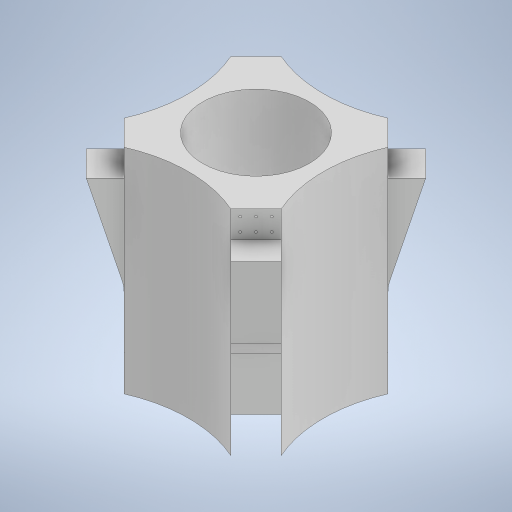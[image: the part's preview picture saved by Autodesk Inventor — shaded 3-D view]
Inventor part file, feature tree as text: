
AUTODESK INVENTOR PART (.ipt)
format: ipt  version: 2023 (Build 270158000, 158)  size: 485,376 bytes
history: native  units: in
note: dims shown in document units (in); Inventor stores cm internally (conversion verified against a paired STEP export)
features: sketch x10, extrude x6, plane x3, pattern_circular x3, projected_geometry x2, other x1, revolve x1, loft x1, fillet x1
ambient origin geometry x8: Origin, YZ Plane, XZ Plane, XY Plane, X Axis, Y Axis, Z Axis, Center Point
bodies: Solid1 (feature_tree)
feature tree (28):
  sketch  "Sketch1"  dims[d0=54.0in d1=54.0in]
  sketch  "Sketch2"  dims[d2=1.0in d3=1.0in]
  extrude  "Extrusion1"  Depth=54.0in
  plane  "Work Plane1"
  other  "Work Axis1"
  revolve  "Revolution3"  [1 undecoded]
  extrude  "Extrusion2"  Depth=0.25in
  pattern_circular  "Circular Pattern1"  [2 undecoded]
  plane  "Work Plane3"
  loft  "Loft1"
  pattern_circular  "Circular Pattern2"  [2 undecoded]
  fillet  "Fillet2"  Radius=12.0in
  extrude  "Extrusion3"  Depth=10.4855in
  extrude  "Extrusion4"  Depth=10.4855in
  extrude  "Extrusion5"  Depth=10.4855in
  pattern_circular  "Circular Pattern3"  [2 undecoded]
  extrude  "Extrusion6"  Depth=15.0in
  plane  "Work Plane2"
  sketch  "Sketch4"  dims[d34=0.25in d35=0.25in]
  sketch  "Sketch5"  dims[d36=0.25in]
  sketch  "Sketch6"  dims[d37=0.25in]
  sketch  "Sketch7"  dims[d38=0.25in]
  sketch  "Sketch8"  dims[d39=0.25in]
  projected_geometry  "Projected Loop1"
  sketch  "Sketch9"  dims[d40=0.25in]
  projected_geometry  "Projected Loop2"
  sketch  "Sketch10"  dims[d41=0.25in]
  sketch  "Sketch11"  dims[d42=2.0in d43=2.0in d44=2.0in d45=2.0in d46=12.0in d47=12.0in d48=12.0in d50=12.0in d51=15.0in d52=15.0in d53=15.0in d54=15.0in d55=17.0in d56=0.0in d64=3.0in d65=4.0in d66=360.0deg d68=0.25in d69=0.25in d70=0.25in d71=0.25in d72=0.25in d73=0.25in d74=0.75in d75=0.75in d76=0.75in d77=0.75in d78=0.75in d79=0.75in d80=0.75in d81=0.75in d82=0.75in d83=0.75in d84=2.0in d85=2.0in d86=2.0in d87=0.0in d88=1.5748in d89=360.0deg d91=-3.0in d92=3.0in d93=3.0in d94=3.5in d95=0.0in d96=90.0deg d97=0.0in d98=90.0deg d99=1.5748in d100=360.0deg d102=4.0in d103=7.0in d104=0.0in d105=3.0in d106=0.0in d107=0.25in d109=0.25in d110=0.25in d112=0.25in d113=0.25in d114=1.0in d115=1.0in d116=1.0in d117=3.0in d118=3.0in d119=1.0in d120=1.0in d121=2.0in d122=2.0in d123=3.0in d124=0.0in d125=1.5748in d126=360.0deg d128=12.0in d129=10.4855in d130=10.4855in d131=80.0in d132=0.0in]
note: 7 required parameter values undecoded (feature->parameter linkage not recoverable at this tier; creation-order binding heuristic only, values carry confidence <= 0.55)